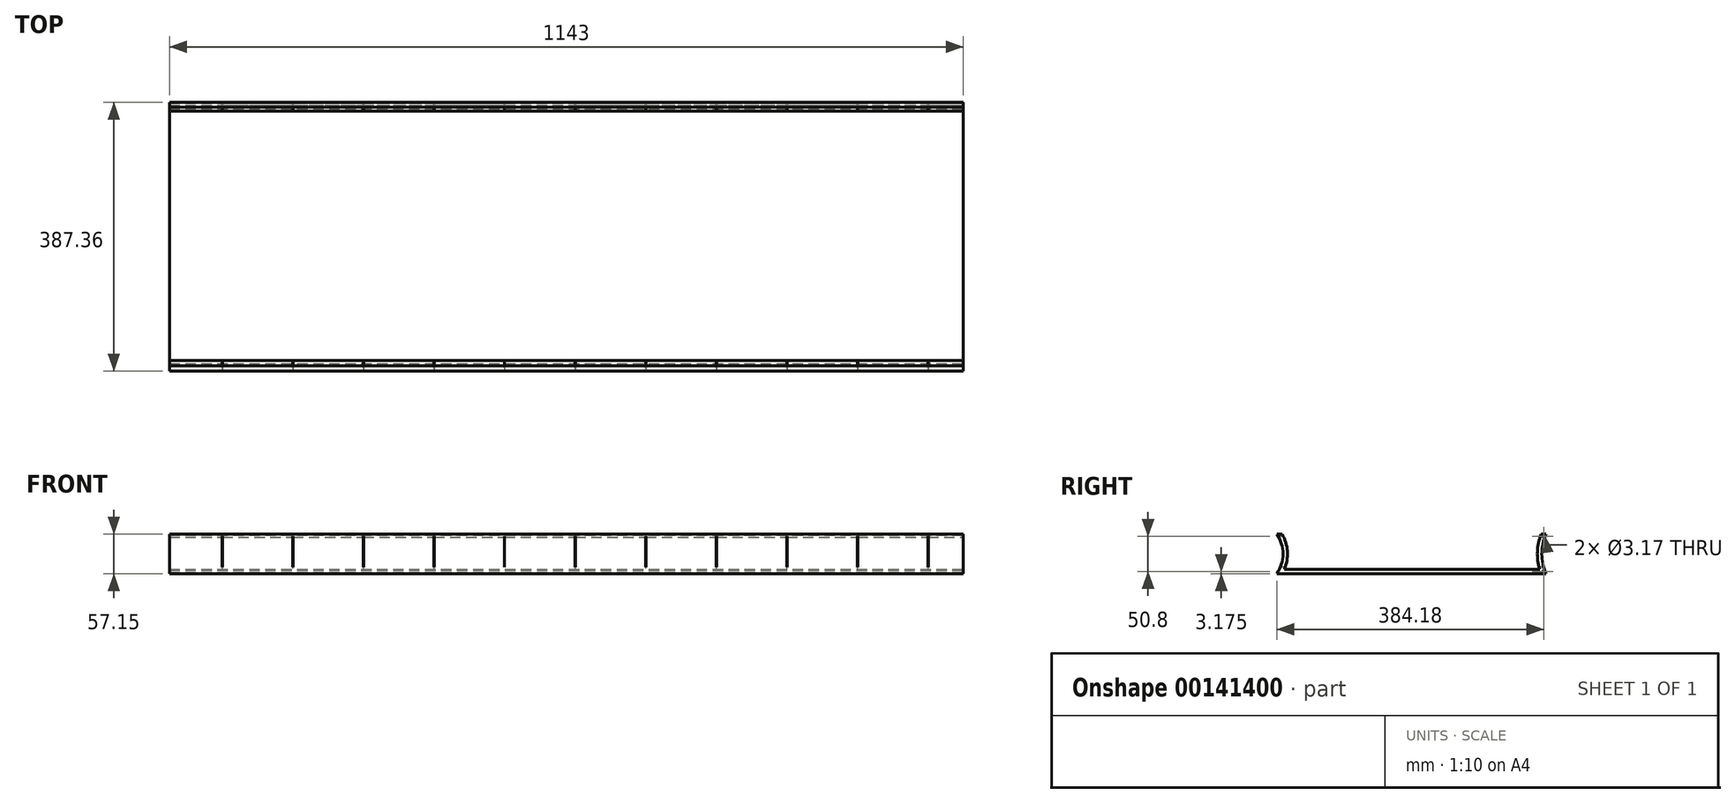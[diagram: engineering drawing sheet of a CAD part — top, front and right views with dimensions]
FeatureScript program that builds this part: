
annotation { "Feature Type Name" : "Feature", "Feature Type Description" : "" }
export const myFeature = defineFeature(function(context is Context, id is Id, definition is map)
    precondition{}
    {
        {
            var Q0;
            Q0=qCreatedBy(makeId("Right.planeOp"),FACE);
            var sketch = newSketch(context, id + "F0", { "sketchPlane" : qUnion([Q0])});
            skLineSegment(sketch, "E0", {"start": v(-193.68, 0) * mm, "end": v(193.68, 0) * mm});
            skArc(sketch, "E1", {"start": v(193.67, 57.15) * mm, "mid": v(187.56, 28.57) * mm, "end": v(193.68, 0) * mm});
            skArc(sketch, "E2", {"start": v(186.77, 57.15) * mm, "mid": v(181.29, 31.94) * mm, "end": v(184.53, 6.35) * mm});
            skLineSegment(sketch, "E3", {"start": v(184.53, 6.35) * mm, "end": v(-183.02, 6.35) * mm});
            skArc(sketch, "E4", {"start": v(-183.02, 6.35) * mm, "mid": v(-178.64, 32.12) * mm, "end": v(-186.18, 57.15) * mm});
            skArc(sketch, "E5", {"start": v(-193.68, 0) * mm, "mid": v(-184.88, 28.57) * mm, "end": v(-193.68, 57.15) * mm});
            skLineSegment(sketch, "E6", {"start": v(-193.68, 57.15) * mm, "end": v(-186.18, 57.15) * mm});
            skLineSegment(sketch, "E7", {"start": v(186.77, 57.15) * mm, "end": v(193.68, 57.15) * mm});
            skSolve(sketch);
        }
        {
            var Q0;
            Q0=qSketchRegion(id+"F0",true);
            extrude(context, id + "F1", {"entities" : qUnion([Q0]), "oppositeDirection" : true, "depth" : 1143 * mm});
        }
        {
            var Q0;
            Q0=makeQuery(id+"F1.opExtrude","CAP_FACE",FACE,{"disambiguationData":[OSD([sQuery(id+"F0.wireOp",EDGE,"E0"),sQuery(id+"F0.wireOp",EDGE,"E1"),sQuery(id+"F0.wireOp",EDGE,"E2"),sQuery(id+"F0.wireOp",EDGE,"E3"),sQuery(id+"F0.wireOp",EDGE,"E4"),sQuery(id+"F0.wireOp",EDGE,"E5"),sQuery(id+"F0.wireOp",EDGE,"E6"),sQuery(id+"F0.wireOp",EDGE,"E7")])],"isStart":true});
            var sketch = newSketch(context, id + "F2", { "sketchPlane" : qUnion([Q0])});
            skCircle(sketch, "E8", {"center": v(190.5, 53.97) * mm, "radius": 1.59 * mm});
            skCircle(sketch, "E9", {"center": v(190.5, 3.17) * mm, "radius": 1.59 * mm});
            skSolve(sketch);
        }
        {
            var Q0;
            Q0=qSketchRegion(id+"F2",true);
            extrude(context, id + "F3", {"entities" : qUnion([Q0]), "operationType" : NewBodyOperationType.REMOVE, "endBound" : BoundingType.THROUGH_ALL, "oppositeDirection" : true, "depth" : 25.4 * mm});
        }
        {
            var Q0;
            Q0=qCreatedBy(makeId("Front.planeOp"),FACE);
            var sketch = newSketch(context, id + "F4", { "sketchPlane" : qUnion([Q0])});
            skLineSegment(sketch, "E10.bottom", {"start": v(-50.8, 9.52) * mm, "end": v(-51.12, 9.52) * mm});
            skLineSegment(sketch, "E10.top", {"start": v(-50.8, 53.97) * mm, "end": v(-51.12, 53.97) * mm});
            skLineSegment(sketch, "E10.left", {"start": v(-50.8, 9.52) * mm, "end": v(-50.8, 53.97) * mm});
            skLineSegment(sketch, "E10.right", {"start": v(-51.12, 9.52) * mm, "end": v(-51.12, 53.97) * mm});
            skLineSegment(sketch, "E11.1.0.0", {"start": v(-152.4, 9.52) * mm, "end": v(-152.72, 9.52) * mm});
            skLineSegment(sketch, "E11.1.0.1", {"start": v(-152.72, 9.52) * mm, "end": v(-152.72, 53.97) * mm});
            skLineSegment(sketch, "E11.1.0.2", {"start": v(-152.4, 9.52) * mm, "end": v(-152.4, 53.97) * mm});
            skLineSegment(sketch, "E11.1.0.3", {"start": v(-152.4, 53.97) * mm, "end": v(-152.72, 53.97) * mm});
            skLineSegment(sketch, "E11.2.0.0", {"start": v(-254, 9.52) * mm, "end": v(-254.32, 9.52) * mm});
            skLineSegment(sketch, "E11.2.0.1", {"start": v(-254.32, 9.52) * mm, "end": v(-254.32, 53.97) * mm});
            skLineSegment(sketch, "E11.2.0.2", {"start": v(-254, 9.52) * mm, "end": v(-254, 53.97) * mm});
            skLineSegment(sketch, "E11.2.0.3", {"start": v(-254, 53.97) * mm, "end": v(-254.32, 53.97) * mm});
            skLineSegment(sketch, "E11.3.0.0", {"start": v(-355.6, 9.52) * mm, "end": v(-355.92, 9.52) * mm});
            skLineSegment(sketch, "E11.3.0.1", {"start": v(-355.92, 9.52) * mm, "end": v(-355.92, 53.97) * mm});
            skLineSegment(sketch, "E11.3.0.2", {"start": v(-355.6, 9.52) * mm, "end": v(-355.6, 53.97) * mm});
            skLineSegment(sketch, "E11.3.0.3", {"start": v(-355.6, 53.97) * mm, "end": v(-355.92, 53.97) * mm});
            skLineSegment(sketch, "E11.4.0.0", {"start": v(-457.2, 9.52) * mm, "end": v(-457.52, 9.52) * mm});
            skLineSegment(sketch, "E11.4.0.1", {"start": v(-457.52, 9.52) * mm, "end": v(-457.52, 53.97) * mm});
            skLineSegment(sketch, "E11.4.0.2", {"start": v(-457.2, 9.52) * mm, "end": v(-457.2, 53.97) * mm});
            skLineSegment(sketch, "E11.4.0.3", {"start": v(-457.2, 53.97) * mm, "end": v(-457.52, 53.97) * mm});
            skLineSegment(sketch, "E11.5.0.0", {"start": v(-558.8, 9.52) * mm, "end": v(-559.12, 9.52) * mm});
            skLineSegment(sketch, "E11.5.0.1", {"start": v(-559.12, 9.52) * mm, "end": v(-559.12, 53.97) * mm});
            skLineSegment(sketch, "E11.5.0.2", {"start": v(-558.8, 9.52) * mm, "end": v(-558.8, 53.97) * mm});
            skLineSegment(sketch, "E11.5.0.3", {"start": v(-558.8, 53.97) * mm, "end": v(-559.12, 53.97) * mm});
            skLineSegment(sketch, "E11.6.0.0", {"start": v(-660.4, 9.52) * mm, "end": v(-660.72, 9.52) * mm});
            skLineSegment(sketch, "E11.6.0.1", {"start": v(-660.72, 9.52) * mm, "end": v(-660.72, 53.97) * mm});
            skLineSegment(sketch, "E11.6.0.2", {"start": v(-660.4, 9.52) * mm, "end": v(-660.4, 53.97) * mm});
            skLineSegment(sketch, "E11.6.0.3", {"start": v(-660.4, 53.97) * mm, "end": v(-660.72, 53.97) * mm});
            skLineSegment(sketch, "E11.7.0.0", {"start": v(-762, 9.52) * mm, "end": v(-762.32, 9.52) * mm});
            skLineSegment(sketch, "E11.7.0.1", {"start": v(-762.32, 9.52) * mm, "end": v(-762.32, 53.97) * mm});
            skLineSegment(sketch, "E11.7.0.2", {"start": v(-762, 9.52) * mm, "end": v(-762, 53.97) * mm});
            skLineSegment(sketch, "E11.7.0.3", {"start": v(-762, 53.97) * mm, "end": v(-762.32, 53.97) * mm});
            skLineSegment(sketch, "E11.8.0.0", {"start": v(-863.6, 9.52) * mm, "end": v(-863.92, 9.52) * mm});
            skLineSegment(sketch, "E11.8.0.1", {"start": v(-863.92, 9.52) * mm, "end": v(-863.92, 53.97) * mm});
            skLineSegment(sketch, "E11.8.0.2", {"start": v(-863.6, 9.52) * mm, "end": v(-863.6, 53.97) * mm});
            skLineSegment(sketch, "E11.8.0.3", {"start": v(-863.6, 53.97) * mm, "end": v(-863.92, 53.97) * mm});
            skLineSegment(sketch, "E11.9.0.0", {"start": v(-965.2, 9.52) * mm, "end": v(-965.52, 9.52) * mm});
            skLineSegment(sketch, "E11.9.0.1", {"start": v(-965.52, 9.52) * mm, "end": v(-965.52, 53.97) * mm});
            skLineSegment(sketch, "E11.9.0.2", {"start": v(-965.2, 9.52) * mm, "end": v(-965.2, 53.97) * mm});
            skLineSegment(sketch, "E11.9.0.3", {"start": v(-965.2, 53.97) * mm, "end": v(-965.52, 53.97) * mm});
            skLineSegment(sketch, "E11.10.0.0", {"start": v(-1066.8, 9.52) * mm, "end": v(-1067.12, 9.52) * mm});
            skLineSegment(sketch, "E11.10.0.1", {"start": v(-1067.12, 9.52) * mm, "end": v(-1067.12, 53.97) * mm});
            skLineSegment(sketch, "E11.10.0.2", {"start": v(-1066.8, 9.52) * mm, "end": v(-1066.8, 53.97) * mm});
            skLineSegment(sketch, "E11.10.0.3", {"start": v(-1066.8, 53.97) * mm, "end": v(-1067.12, 53.97) * mm});
            skLineSegment(sketch, "E11.11.0.0", {"start": v(-1168.4, 9.52) * mm, "end": v(-1168.72, 9.52) * mm});
            skLineSegment(sketch, "E11.11.0.1", {"start": v(-1168.72, 9.52) * mm, "end": v(-1168.72, 53.97) * mm});
            skLineSegment(sketch, "E11.11.0.2", {"start": v(-1168.4, 9.52) * mm, "end": v(-1168.4, 53.97) * mm});
            skLineSegment(sketch, "E11.11.0.3", {"start": v(-1168.4, 53.97) * mm, "end": v(-1168.72, 53.97) * mm});
            skLineSegment(sketch, "E11.direction1", {"start": v(-51.12, 9.52) * mm, "end": v(-152.72, 9.52) * mm, "construction": true});
            skSolve(sketch);
        }
        {
            var Q0;
            Q0=qSketchRegion(id+"F4",true);
            var Q1;
            Q1=makeQuery(id+"F1.opExtrude","SWEPT_FACE",FACE,{"disambiguationData":[OSD([sQuery(id+"F0.wireOp",EDGE,"E1")])]});
            var Q2;
            Q2=makeQuery(id+"F1.opExtrude","SWEPT_FACE",FACE,{"disambiguationData":[OSD([sQuery(id+"F0.wireOp",EDGE,"E5")])]});
            extrude(context, id + "F5", {"entities" : qUnion([Q0]), "operationType" : NewBodyOperationType.REMOVE, "endBound" : BoundingType.UP_TO_SURFACE, "oppositeDirection" : true, "endBoundEntityFace" : qUnion([Q1]), "depth" : 25.4 * mm, "hasSecondDirection" : true, "secondDirectionBound" : BoundingType.UP_TO_SURFACE, "secondDirectionOppositeDirection" : false, "secondDirectionBoundEntityFace" : qUnion([Q2]), "secondDirectionDepth" : 25.4 * mm});
        }
    });
